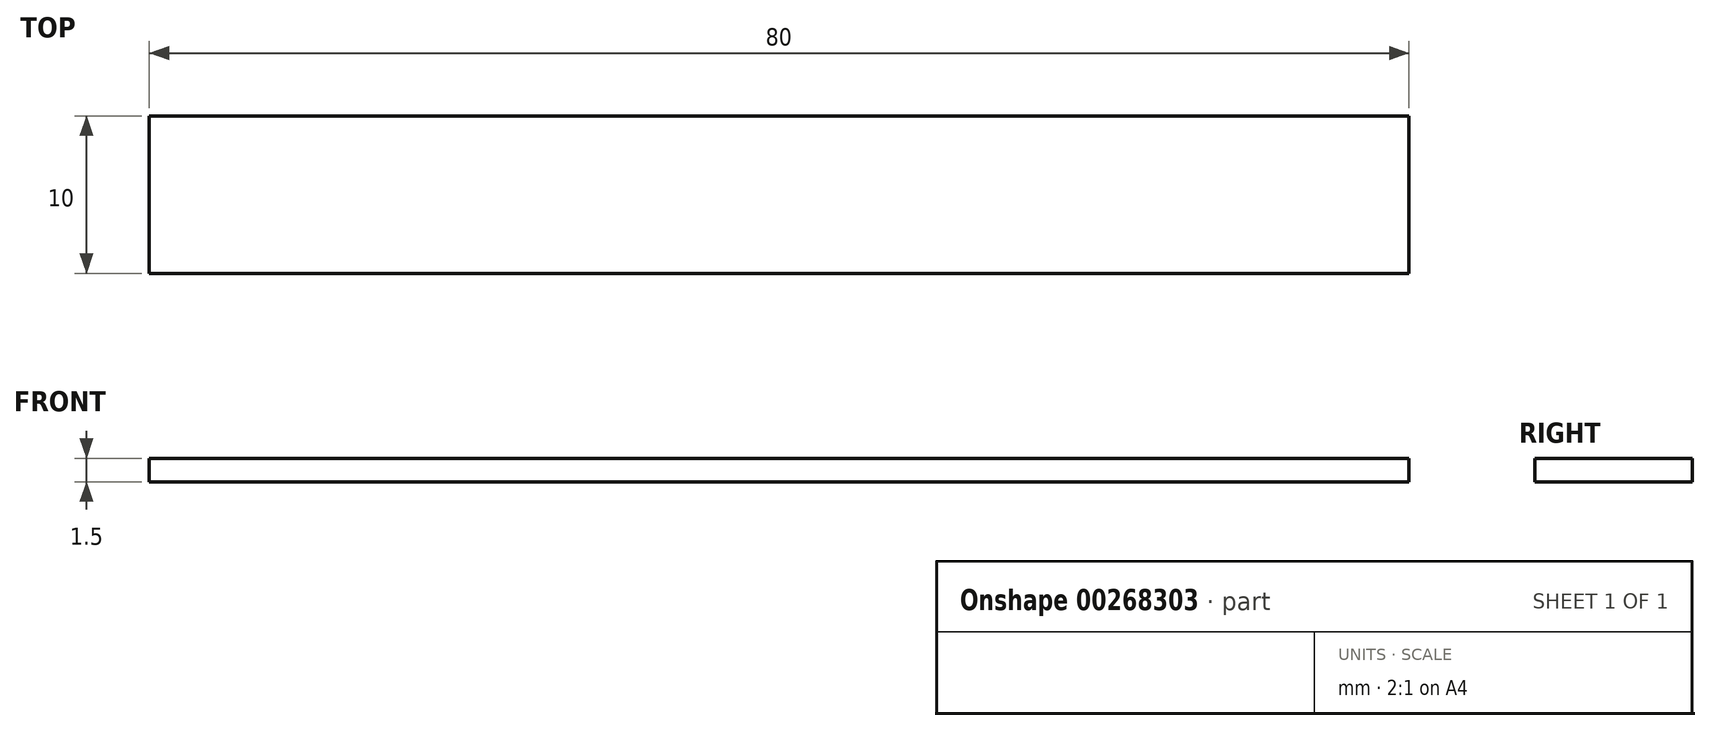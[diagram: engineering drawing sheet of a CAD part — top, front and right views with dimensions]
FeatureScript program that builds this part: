
annotation { "Feature Type Name" : "Feature", "Feature Type Description" : "" }
export const myFeature = defineFeature(function(context is Context, id is Id, definition is map)
    precondition{}
    {
        {
            var Q0;
            Q0=qCreatedBy(makeId("Top.planeOp"),FACE);
            var sketch = newSketch(context, id + "F0", { "sketchPlane" : qUnion([Q0])});
            skLineSegment(sketch, "E0.bottom", {"start": v(0, 0) * mm, "end": v(80, 0) * mm});
            skLineSegment(sketch, "E0.top", {"start": v(0, -10) * mm, "end": v(80, -10) * mm});
            skLineSegment(sketch, "E0.left", {"start": v(0, 0) * mm, "end": v(0, -10) * mm});
            skLineSegment(sketch, "E0.right", {"start": v(80, 0) * mm, "end": v(80, -10) * mm});
            skSolve(sketch);
        }
        {
            var Q0;
            Q0 = qSketchRegion(id + "F0", true);
            extrude(context, id + "F1", {"entities" : qUnion([Q0]), "depth" : 1.5 * mm});
        }
    });
